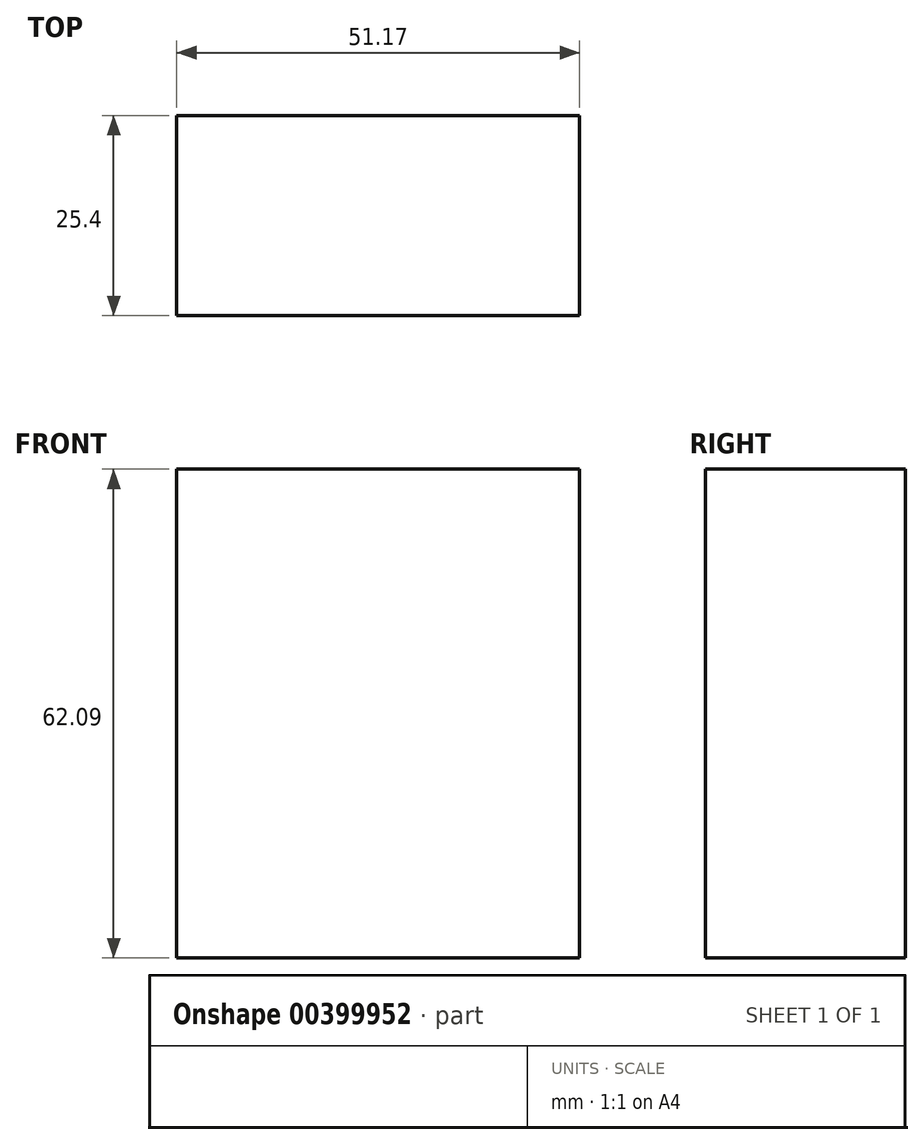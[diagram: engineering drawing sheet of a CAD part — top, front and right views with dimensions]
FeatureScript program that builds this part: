
annotation { "Feature Type Name" : "Feature", "Feature Type Description" : "" }
export const myFeature = defineFeature(function(context is Context, id is Id, definition is map)
    precondition{}
    {
        {
            var Q0;
            Q0=qCreatedBy(makeId("Front.planeOp"),FACE);
            var sketch = newSketch(context, id + "F0", { "sketchPlane" : qUnion([Q0])});
            skLineSegment(sketch, "E0.bottom", {"start": v(0, 0) * mm, "end": v(0, 0) * mm});
            skLineSegment(sketch, "E0.top", {"start": v(0, 0) * mm, "end": v(0, 0) * mm});
            skLineSegment(sketch, "E0.left", {"start": v(0, 0) * mm, "end": v(0, 0) * mm});
            skLineSegment(sketch, "E0.right", {"start": v(0, 0) * mm, "end": v(0, 0) * mm});
            skLineSegment(sketch, "E1.bottom", {"start": v(0, 62.09) * mm, "end": v(51.17, 62.09) * mm});
            skLineSegment(sketch, "E1.top", {"start": v(0, 0) * mm, "end": v(51.17, 0) * mm});
            skLineSegment(sketch, "E1.left", {"start": v(0, 62.09) * mm, "end": v(0, 0) * mm});
            skLineSegment(sketch, "E1.right", {"start": v(51.17, 62.09) * mm, "end": v(51.17, 0) * mm});
            skSolve(sketch);
        }
        {
            var Q0;
            Q0=makeQuery(id+"F0.imprint","IMPRINT",FACE,{"disambiguationData":[TD([[makeQuery(id+"F0.imprint","IMPRINT",EDGE,{"derivedFrom":sQuery(id+"F0.wireOp",EDGE,"E1.bottom")}),-1.0]])]});
            extrude(context, id + "F1", {"entities" : qUnion([Q0]), "oppositeDirection" : true, "depth" : 25.4 * mm});
        }
    });
